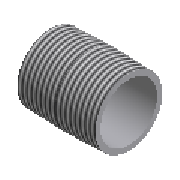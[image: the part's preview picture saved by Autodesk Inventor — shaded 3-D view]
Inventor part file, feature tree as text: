
AUTODESK INVENTOR PART (.ipt)
format: ipt  version: 2023.2 (Build 272271030, 271C)  size: 179,200 bytes
history: native  units: mm (DEFAULTED — no unit token found)
features: other x6, revolve x1, sketch x1
ambient origin geometry x8: Origin, YZ Plane, XZ Plane, XY Plane, X Axis, Y Axis, Z Axis, Center Point
bodies: Solid1 (feature_tree)
feature tree (8):
  revolve  "Revolution1"  Angle=90.0deg
  other  "Work Point1"
  other  "Work Axis1"
  other  "Work Point2"
  other  "Work Axis2"
  other  "Work Point3"
  other  "Work Point4"
  sketch  "Sketch1"  dims[d0=16.1mm d12=90.0deg d1=0.312398mm d2=29.0mm d3=0.0mm d4=0.0mm d5=0.0mm d6=0.0mm d7=8.16mm d8=20.955mm]
